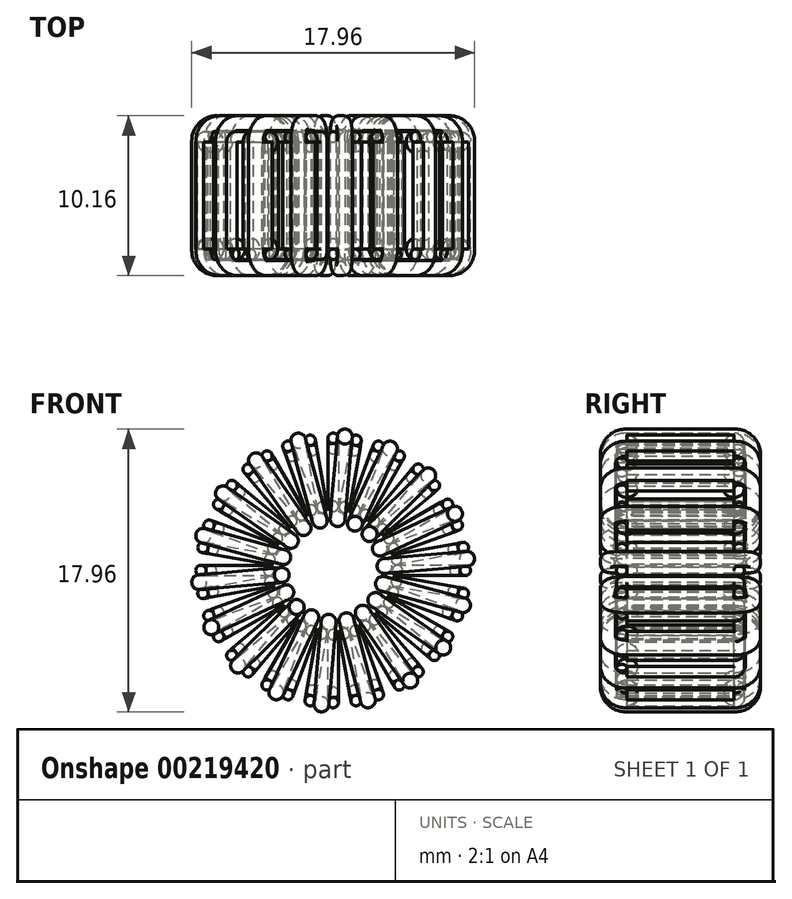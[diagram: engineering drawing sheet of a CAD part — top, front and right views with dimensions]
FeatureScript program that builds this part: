
annotation { "Feature Type Name" : "Feature", "Feature Type Description" : "" }
export const myFeature = defineFeature(function(context is Context, id is Id, definition is map)
    precondition{}
    {
        {
            assignVariable(context, id + "F0", {"variableType" : VariableType.NUMBER, "name" : "NumTurns1", "numberValue" : 36});
        }
        {
            assignVariable(context, id + "F1", {"variableType" : VariableType.NUMBER, "name" : "NumTurns2", "numberValue" : 18});
        }
        {
            assignVariable(context, id + "F2", {"variableType" : VariableType.ANGLE, "name" : "PlaneShift", "angleValue" : (360 / getVariable(context, 'NumTurns1')) / 2 * degree});
        }
        {
            var Q0;
            Q0=qCreatedBy(makeId("Top.planeOp"),FACE);
            var sketch = newSketch(context, id + "F3", { "sketchPlane" : qUnion([Q0])});
            skLineSegment(sketch, "E0.bottom", {"start": v(8.06, -3.73) * mm, "end": v(4.41, -3.73) * mm});
            skLineSegment(sketch, "E0.top", {"start": v(8.07, 3.73) * mm, "end": v(4.4, 3.73) * mm});
            skLineSegment(sketch, "E0.left", {"start": v(8.4, -3.4) * mm, "end": v(8.4, 3.4) * mm});
            skLineSegment(sketch, "E0.right", {"start": v(4.08, -3.4) * mm, "end": v(4.08, 3.4) * mm});
            skPoint(sketch, "E0.middle", {"position": v(6.24, 0) * mm});
            skPoint(sketch, "E1.visualSharp", {"position": v(4.08, 3.73) * mm});
            skArc(sketch, "E1.filletArc", {"start": v(4.4, 3.73) * mm, "mid": v(4.18, 3.63) * mm, "end": v(4.08, 3.4) * mm});
            skPoint(sketch, "E2.visualSharp", {"position": v(8.4, 3.73) * mm});
            skArc(sketch, "E2.filletArc", {"start": v(8.4, 3.4) * mm, "mid": v(8.3, 3.63) * mm, "end": v(8.07, 3.73) * mm});
            skPoint(sketch, "E3.visualSharp", {"position": v(8.4, -3.73) * mm});
            skArc(sketch, "E3.filletArc", {"start": v(8.06, -3.73) * mm, "mid": v(8.3, -3.63) * mm, "end": v(8.4, -3.4) * mm});
            skPoint(sketch, "E4.visualSharp", {"position": v(4.08, -3.73) * mm});
            skArc(sketch, "E4.filletArc", {"start": v(4.08, -3.4) * mm, "mid": v(4.18, -3.63) * mm, "end": v(4.41, -3.73) * mm});
            skSolve(sketch);
        }
        {
            var Q0;
            Q0=qCreatedBy(makeId("Front.planeOp"),FACE);
            var sketch = newSketch(context, id + "F4", { "sketchPlane" : qUnion([Q0])});
            skCircle(sketch, "E5", {"center": v(4.08, 0) * mm, "radius": 0.33 * mm});
            skSolve(sketch);
        }
        {
            var Q0;
            Q0=makeQuery(id+"F4.imprint","IMPRINT",FACE,{"disambiguationData":[TD([[makeQuery(id+"F4.imprint","IMPRINT",EDGE,{"derivedFrom":sQuery(id+"F4.wireOp",EDGE,"E5")}),1.0]])]});
            var Q1;
            Q1=sQuery(id+"F3.wireOp",EDGE,"E0.right");
            var Q2;
            Q2=sQuery(id+"F3.wireOp",EDGE,"E0.top");
            var Q3;
            Q3=sQuery(id+"F3.wireOp",EDGE,"E1.filletArc");
            var Q4;
            Q4=sQuery(id+"F3.wireOp",EDGE,"E2.filletArc");
            var Q5;
            Q5=sQuery(id+"F3.wireOp",EDGE,"E0.left");
            var Q6;
            Q6=sQuery(id+"F3.wireOp",EDGE,"E3.filletArc");
            var Q7;
            Q7=sQuery(id+"F3.wireOp",EDGE,"E0.bottom");
            var Q8;
            Q8=sQuery(id+"F3.wireOp",EDGE,"E4.filletArc");
            sweep(context, id + "F5", {"profiles" : qUnion([Q0]), "path" : qUnion([Q1, Q2, Q3, Q4, Q5, Q6, Q7, Q8])});
        }
        {
            var Q0;
            Q0=qCreatedBy(makeId("Top.planeOp"),FACE);
            var sketch = newSketch(context, id + "F6", { "sketchPlane" : qUnion([Q0])});
            skLineSegment(sketch, "E6", {"start": v(0, 4.82) * mm, "end": v(0, -5.5) * mm, "construction": true});
            skSolve(sketch);
        }
        {
            var Q0;
            Q0=makeQuery(id+"F5.opSweep","SWEPT_BODY",BODY,{"disambiguationData":[OSD([sQuery(id+"F3.wireOp",EDGE,"E2.filletArc"),sQuery(id+"F4.wireOp",EDGE,"E5")])]});
            var Q1;
            Q1=sQuery(id+"F6.wireOp",EDGE,"E6");
            circularPattern(context, id + "F7", {"entities" : qUnion([Q0]), "axis" : qUnion([Q1]), "angle" : 360 * degree, "instanceCount" : getVariable(context, 'NumTurns1'), "equalSpace" : true});
        }
        {
            var Q0;
            Q0=qCreatedBy(makeId("Top.planeOp"),FACE);
            var Q1;
            Q1 = qBodyType(qCreatedBy(id + "F6" ,EDGE), BodyType.WIRE);
            cPlane(context, id + "F8", {"entities" : qUnion([Q0, Q1]), "cplaneType" : CPlaneType.LINE_ANGLE, "offset" : 25.4 * mm, "angle" : getVariable(context, 'PlaneShift'), "width" : 152.4 * mm, "height" : 152.4 * mm});
        }
        {
            var Q0;
            Q0=qCreatedBy(id+"F8.planeOp",FACE);
            var sketch = newSketch(context, id + "F9", { "sketchPlane" : qUnion([Q0])});
            skLineSegment(sketch, "E7.bottom", {"start": v(7.4, 4.61) * mm, "end": v(4.4, 4.61) * mm});
            skLineSegment(sketch, "E7.top", {"start": v(7.4, -4.61) * mm, "end": v(4.4, -4.61) * mm});
            skLineSegment(sketch, "E7.left", {"start": v(8.54, 3.48) * mm, "end": v(8.54, -3.48) * mm});
            skLineSegment(sketch, "E7.right", {"start": v(3.28, 3.48) * mm, "end": v(3.28, -3.48) * mm});
            skPoint(sketch, "E7.middle", {"position": v(5.9, 0) * mm});
            skPoint(sketch, "E8.visualSharp", {"position": v(3.28, -4.61) * mm});
            skArc(sketch, "E8.filletArc", {"start": v(3.28, -3.48) * mm, "mid": v(3.6, -4.28) * mm, "end": v(4.4, -4.61) * mm});
            skPoint(sketch, "E9.visualSharp", {"position": v(8.54, -4.61) * mm});
            skArc(sketch, "E9.filletArc", {"start": v(7.4, -4.61) * mm, "mid": v(8.2, -4.28) * mm, "end": v(8.54, -3.48) * mm});
            skPoint(sketch, "E10.visualSharp", {"position": v(3.28, 4.61) * mm});
            skArc(sketch, "E10.filletArc", {"start": v(4.4, 4.61) * mm, "mid": v(3.6, 4.28) * mm, "end": v(3.28, 3.48) * mm});
            skPoint(sketch, "E11.visualSharp", {"position": v(8.54, 4.61) * mm});
            skArc(sketch, "E11.filletArc", {"start": v(8.54, 3.48) * mm, "mid": v(8.2, 4.28) * mm, "end": v(7.4, 4.61) * mm});
            skSolve(sketch);
        }
        {
            var Q0;
            Q0=qCreatedBy(makeId("Front.planeOp"),FACE);
            var sketch = newSketch(context, id + "F10", { "sketchPlane" : qUnion([Q0])});
            skCircle(sketch, "E12", {"center": v(3.26, 0.29) * mm, "radius": 0.47 * mm});
            skSolve(sketch);
        }
        {
            var Q0;
            Q0=makeQuery(id+"F10.imprint","IMPRINT",FACE,{"disambiguationData":[TD([[makeQuery(id+"F10.imprint","IMPRINT",EDGE,{"derivedFrom":sQuery(id+"F10.wireOp",EDGE,"E12")}),1.0]])]});
            var Q1;
            Q1=sQuery(id+"F9.wireOp",EDGE,"E7.top");
            var Q2;
            Q2=sQuery(id+"F9.wireOp",EDGE,"E8.filletArc");
            var Q3;
            Q3=sQuery(id+"F9.wireOp",EDGE,"E7.right");
            var Q4;
            Q4=sQuery(id+"F9.wireOp",EDGE,"E10.filletArc");
            var Q5;
            Q5=sQuery(id+"F9.wireOp",EDGE,"E7.bottom");
            var Q6;
            Q6=sQuery(id+"F9.wireOp",EDGE,"E11.filletArc");
            var Q7;
            Q7=sQuery(id+"F9.wireOp",EDGE,"E7.left");
            var Q8;
            Q8=sQuery(id+"F9.wireOp",EDGE,"E9.filletArc");
            sweep(context, id + "F11", {"profiles" : qUnion([Q0]), "path" : qUnion([Q1, Q2, Q3, Q4, Q5, Q6, Q7, Q8])});
        }
        {
            var Q0;
            Q0=makeQuery(id+"F11.opSweep","SWEPT_BODY",BODY,{"disambiguationData":[OSD([sQuery(id+"F9.wireOp",EDGE,"E9.filletArc"),sQuery(id+"F10.wireOp",EDGE,"E12")])]});
            var Q1;
            Q1=sQuery(id+"F6.wireOp",EDGE,"E6");
            circularPattern(context, id + "F12", {"entities" : qUnion([Q0]), "axis" : qUnion([Q1]), "angle" : 360 * degree, "instanceCount" : getVariable(context, 'NumTurns2'), "equalSpace" : true});
        }
    });
